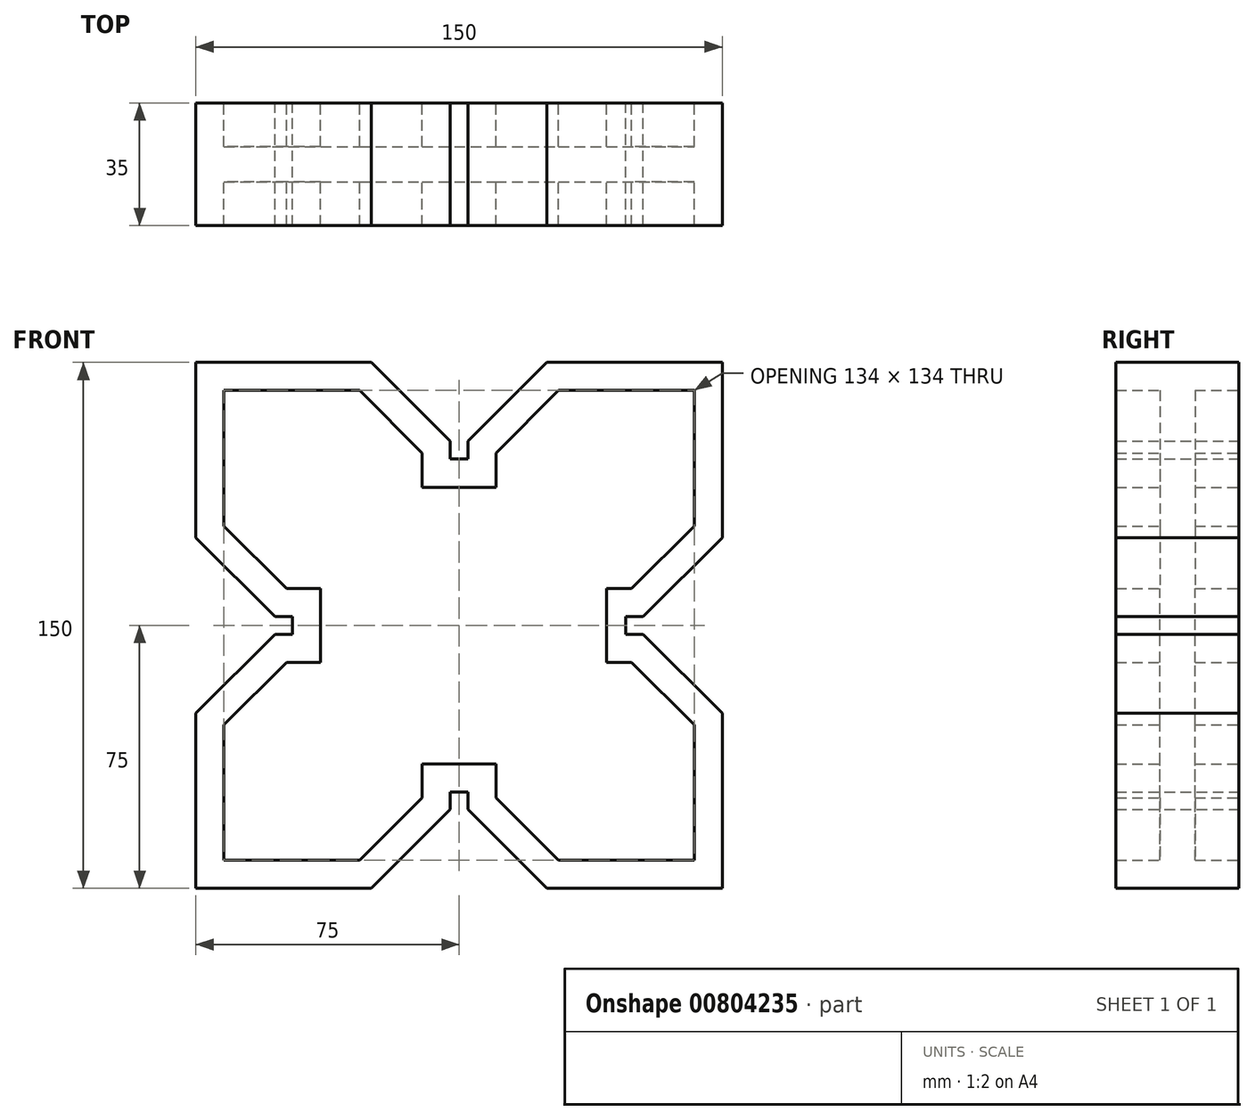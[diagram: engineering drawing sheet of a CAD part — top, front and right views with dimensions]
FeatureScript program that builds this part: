
annotation { "Feature Type Name" : "Feature", "Feature Type Description" : "" }
export const myFeature = defineFeature(function(context is Context, id is Id, definition is map)
    precondition{}
    {
        {
            var Q0;
            Q0=qCreatedBy(makeId("Front.planeOp"),FACE);
            var sketch = newSketch(context, id + "F0", { "sketchPlane" : qUnion([Q0])});
            skLineSegment(sketch, "E0.bottom", {"start": v(0, 0) * mm, "end": v(50, 0) * mm});
            skLineSegment(sketch, "E0.top", {"start": v(0, 150) * mm, "end": v(50, 150) * mm});
            skLineSegment(sketch, "E0.left", {"start": v(0, 0) * mm, "end": v(0, 50) * mm});
            skLineSegment(sketch, "E0.right", {"start": v(150, 0) * mm, "end": v(150, 50) * mm});
            skLineSegment(sketch, "E1", {"start": v(50, 150) * mm, "end": v(72.5, 127.5) * mm});
            skLineSegment(sketch, "E2", {"start": v(0, 100) * mm, "end": v(22.5, 77.5) * mm});
            skLineSegment(sketch, "E3", {"start": v(100, 150) * mm, "end": v(77.5, 127.5) * mm});
            skLineSegment(sketch, "E4", {"start": v(50, 0) * mm, "end": v(72.5, 22.5) * mm});
            skPoint(sketch, "E4.startSnap0", {"position": v(50, 100) * mm});
            skLineSegment(sketch, "E5.bottom", {"start": v(122.5, 72.5) * mm, "end": v(127.5, 72.5) * mm});
            skLineSegment(sketch, "E5.top", {"start": v(122.5, 77.5) * mm, "end": v(127.5, 77.5) * mm});
            skLineSegment(sketch, "E5.left", {"start": v(122.5, 72.5) * mm, "end": v(122.5, 77.5) * mm});
            skPoint(sketch, "E5.middle", {"position": v(125, 75) * mm});
            skLineSegment(sketch, "E6.bottom", {"start": v(77.5, 27.5) * mm, "end": v(72.5, 27.5) * mm});
            skLineSegment(sketch, "E6.left", {"start": v(77.5, 27.5) * mm, "end": v(77.5, 22.5) * mm});
            skLineSegment(sketch, "E6.right", {"start": v(72.5, 27.5) * mm, "end": v(72.5, 22.5) * mm});
            skPoint(sketch, "E6.middle", {"position": v(75, 25) * mm});
            skPoint(sketch, "E6.middle.positionSnap0", {"position": v(75, 0) * mm});
            skPoint(sketch, "E6.centerSnap0", {"position": v(75, 0) * mm});
            skLineSegment(sketch, "E7.bottom", {"start": v(27.5, 77.5) * mm, "end": v(22.5, 77.5) * mm});
            skLineSegment(sketch, "E7.top", {"start": v(27.5, 72.5) * mm, "end": v(22.5, 72.5) * mm});
            skLineSegment(sketch, "E7.left", {"start": v(27.5, 77.5) * mm, "end": v(27.5, 72.5) * mm});
            skPoint(sketch, "E7.middle", {"position": v(25, 75) * mm});
            skLineSegment(sketch, "E8.bottom", {"start": v(77.5, 122.5) * mm, "end": v(72.5, 122.5) * mm});
            skLineSegment(sketch, "E8.left", {"start": v(77.5, 122.5) * mm, "end": v(77.5, 127.5) * mm});
            skLineSegment(sketch, "E8.right", {"start": v(72.5, 122.5) * mm, "end": v(72.5, 127.5) * mm});
            skPoint(sketch, "E8.middle", {"position": v(75, 125) * mm});
            skLineSegment(sketch, "E9.trimOffspring", {"start": v(100, 150) * mm, "end": v(150, 150) * mm});
            skLineSegment(sketch, "E10.trimOffspring", {"start": v(150, 100) * mm, "end": v(150, 150) * mm});
            skLineSegment(sketch, "E11.trimOffspring", {"start": v(100, 0) * mm, "end": v(150, 0) * mm});
            skLineSegment(sketch, "E12.trimOffspring", {"start": v(0, 100) * mm, "end": v(0, 150) * mm});
            skLineSegment(sketch, "E13.trimOffspring", {"start": v(22.5, 72.5) * mm, "end": v(0, 50) * mm});
            skLineSegment(sketch, "E14.trimOffspring", {"start": v(127.5, 72.5) * mm, "end": v(150, 50) * mm});
            skLineSegment(sketch, "E15.trimOffspring", {"start": v(127.5, 77.5) * mm, "end": v(150, 100) * mm});
            skLineSegment(sketch, "E16.trimOffspring", {"start": v(77.5, 22.5) * mm, "end": v(100, 0) * mm});
            skLineSegment(sketch, "E17", {"start": v(8, 142) * mm, "end": v(46.69, 142) * mm});
            skLineSegment(sketch, "E18", {"start": v(46.69, 142) * mm, "end": v(64.5, 124.19) * mm});
            skLineSegment(sketch, "E19", {"start": v(64.5, 124.19) * mm, "end": v(64.5, 114.36) * mm});
            skLineSegment(sketch, "E20", {"start": v(64.5, 114.36) * mm, "end": v(85.5, 114.36) * mm});
            skLineSegment(sketch, "E21", {"start": v(85.5, 114.36) * mm, "end": v(85.5, 124.19) * mm});
            skLineSegment(sketch, "E22", {"start": v(85.5, 124.19) * mm, "end": v(103.31, 142) * mm});
            skLineSegment(sketch, "E23", {"start": v(103.31, 142) * mm, "end": v(142, 142) * mm});
            skLineSegment(sketch, "E24", {"start": v(142, 142) * mm, "end": v(142, 103.31) * mm});
            skLineSegment(sketch, "E25", {"start": v(8, 142) * mm, "end": v(8, 103.31) * mm});
            skLineSegment(sketch, "E26", {"start": v(8, 103.31) * mm, "end": v(25.81, 85.5) * mm});
            skLineSegment(sketch, "E27", {"start": v(25.81, 85.5) * mm, "end": v(35.5, 85.5) * mm});
            skLineSegment(sketch, "E28", {"start": v(35.5, 85.5) * mm, "end": v(35.5, 64.5) * mm});
            skLineSegment(sketch, "E29", {"start": v(35.5, 64.5) * mm, "end": v(25.81, 64.5) * mm});
            skLineSegment(sketch, "E30", {"start": v(25.81, 64.5) * mm, "end": v(8, 46.69) * mm});
            skLineSegment(sketch, "E31", {"start": v(8, 46.69) * mm, "end": v(8, 8) * mm});
            skLineSegment(sketch, "E32", {"start": v(8, 8) * mm, "end": v(46.69, 8) * mm});
            skLineSegment(sketch, "E33", {"start": v(46.69, 8) * mm, "end": v(64.5, 25.81) * mm});
            skLineSegment(sketch, "E34", {"start": v(64.5, 25.81) * mm, "end": v(64.5, 35.5) * mm});
            skLineSegment(sketch, "E35", {"start": v(64.5, 35.5) * mm, "end": v(85.5, 35.5) * mm});
            skLineSegment(sketch, "E36", {"start": v(85.5, 25.81) * mm, "end": v(85.5, 35.5) * mm});
            skLineSegment(sketch, "E37", {"start": v(85.5, 25.81) * mm, "end": v(103.31, 8) * mm});
            skLineSegment(sketch, "E38", {"start": v(103.31, 8) * mm, "end": v(142, 8) * mm});
            skLineSegment(sketch, "E39", {"start": v(142, 8) * mm, "end": v(142, 46.69) * mm});
            skLineSegment(sketch, "E40", {"start": v(142, 46.69) * mm, "end": v(124.19, 64.5) * mm});
            skLineSegment(sketch, "E41", {"start": v(124.19, 64.5) * mm, "end": v(117, 64.5) * mm});
            skLineSegment(sketch, "E42", {"start": v(117, 64.5) * mm, "end": v(117, 85.5) * mm});
            skLineSegment(sketch, "E43", {"start": v(117, 85.5) * mm, "end": v(124.19, 85.5) * mm});
            skLineSegment(sketch, "E44", {"start": v(142, 103.31) * mm, "end": v(124.19, 85.5) * mm});
            skSolve(sketch);
        }
        {
            var Q0;
            Q0=makeQuery(id+"F0.imprint","IMPRINT",FACE,{"disambiguationData":[TD([[makeQuery(id+"F0.imprint","IMPRINT",EDGE,{"derivedFrom":sQuery(id+"F0.wireOp",EDGE,"E0.bottom")}),1.0]])]});
            extrude(context, id + "F1", {"entities" : qUnion([Q0]), "endBound" : BoundingType.SYMMETRIC, "depth" : 35 * mm, "offsetDistance" : 25 * mm});
        }
        {
            var Q0;
            Q0=makeQuery(id+"F0.imprint","IMPRINT",FACE,{"disambiguationData":[TD([[makeQuery(id+"F0.imprint","IMPRINT",EDGE,{"derivedFrom":sQuery(id+"F0.wireOp",EDGE,"E17")}),-1.0]])]});
            extrude(context, id + "F2", {"entities" : qUnion([Q0]), "operationType" : NewBodyOperationType.ADD, "endBound" : BoundingType.SYMMETRIC, "depth" : 10 * mm, "offsetDistance" : 25 * mm});
        }
    });
